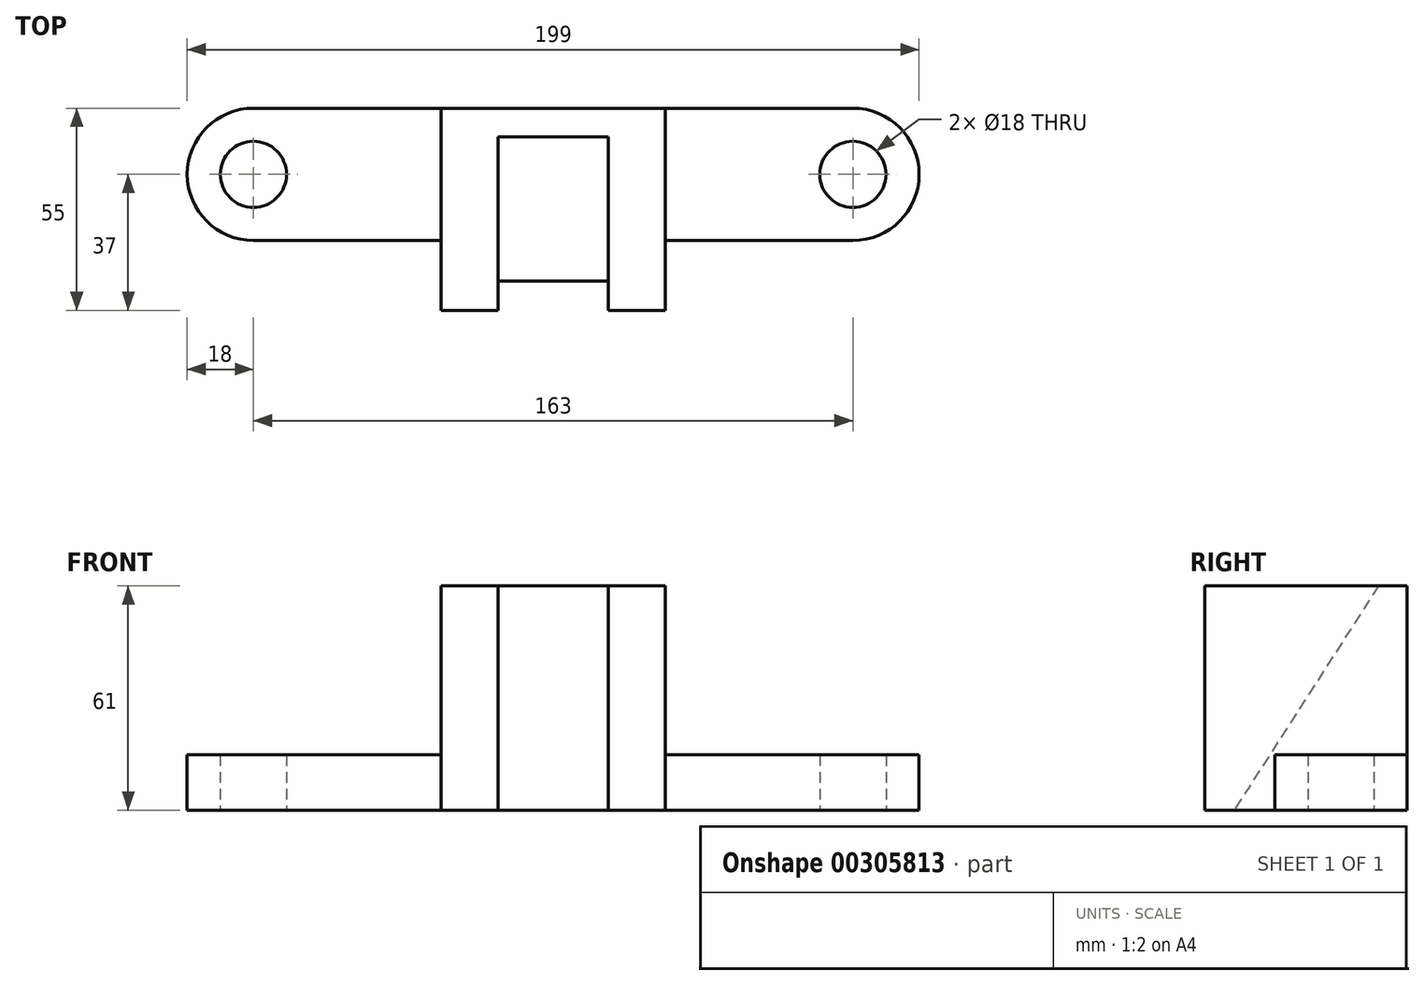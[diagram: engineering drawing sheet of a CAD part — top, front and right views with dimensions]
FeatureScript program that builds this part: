
annotation { "Feature Type Name" : "Feature", "Feature Type Description" : "" }
export const myFeature = defineFeature(function(context is Context, id is Id, definition is map)
    precondition{}
    {
        {
            var Q0;
            Q0=qCreatedBy(makeId("Top.planeOp"),FACE);
            var sketch = newSketch(context, id + "F0", { "sketchPlane" : qUnion([Q0])});
            skLineSegment(sketch, "E0.bottom", {"start": v(-30.5, 27.5) * mm, "end": v(30.5, 27.5) * mm});
            skLineSegment(sketch, "E0.top", {"start": v(-30.5, -27.5) * mm, "end": v(30.5, -27.5) * mm});
            skLineSegment(sketch, "E0.left", {"start": v(-30.5, 27.5) * mm, "end": v(-30.5, -27.5) * mm});
            skLineSegment(sketch, "E0.right", {"start": v(30.5, 27.5) * mm, "end": v(30.5, -27.5) * mm});
            skSolve(sketch);
        }
        {
            var Q0;
            Q0 = qSketchRegion(id + "F0", true);
            extrude(context, id + "F1", {"entities" : qUnion([Q0]), "depth" : 61 * mm});
        }
        {
            var Q0;
            Q0=makeQuery(id+"F1.opExtrude","CAP_FACE",FACE,{"disambiguationData":[OSD([sQuery(id+"F0.wireOp",EDGE,"E0.bottom"),sQuery(id+"F0.wireOp",EDGE,"E0.top"),sQuery(id+"F0.wireOp",EDGE,"E0.left"),sQuery(id+"F0.wireOp",EDGE,"E0.right")])],"isStart":false});
            var sketch = newSketch(context, id + "F2", { "sketchPlane" : qUnion([Q0])});
            skLineSegment(sketch, "E1.bottom", {"start": v(-15, -27.5) * mm, "end": v(15, -27.5) * mm});
            skLineSegment(sketch, "E1.top", {"start": v(-15, 19.75) * mm, "end": v(15, 19.75) * mm});
            skLineSegment(sketch, "E1.left", {"start": v(-15, -27.5) * mm, "end": v(-15, 19.75) * mm});
            skLineSegment(sketch, "E1.right", {"start": v(15, -27.5) * mm, "end": v(15, 19.75) * mm});
            skSolve(sketch);
        }
        {
            var Q0;
            Q0 = qSketchRegion(id + "F2", true);
            extrude(context, id + "F3", {"entities" : qUnion([Q0]), "operationType" : NewBodyOperationType.REMOVE, "oppositeDirection" : true, "depth" : 61 * mm});
        }
        {
            var Q0;
            Q0=makeQuery(id+"F1.opExtrude","CAP_FACE",FACE,{"disambiguationData":[OSD([sQuery(id+"F0.wireOp",EDGE,"E0.bottom"),sQuery(id+"F0.wireOp",EDGE,"E0.top"),sQuery(id+"F0.wireOp",EDGE,"E0.left"),sQuery(id+"F0.wireOp",EDGE,"E0.right")])],"isStart":true});
            var sketch = newSketch(context, id + "F4", { "sketchPlane" : qUnion([Q0])});
            skLineSegment(sketch, "E2", {"start": v(-30.5, -27.5) * mm, "end": v(-81.5, -27.5) * mm});
            skLineSegment(sketch, "E3", {"start": v(-30.5, 8.5) * mm, "end": v(-81.5, 8.5) * mm});
            skArc(sketch, "E4", {"start": v(-81.5, 8.5) * mm, "mid": v(-99.5, -9.5) * mm, "end": v(-81.5, -27.5) * mm});
            skCircle(sketch, "E5", {"center": v(-81.5, -9.5) * mm, "radius": 9 * mm});
            skLineSegment(sketch, "E6.MirrorCS", {"start": v(30.5, -27.5) * mm, "end": v(81.5, -27.5) * mm});
            skArc(sketch, "E7.MirrorCS", {"start": v(81.5, 8.5) * mm, "mid": v(99.5, -9.5) * mm, "end": v(81.5, -27.5) * mm});
            skLineSegment(sketch, "E8.MirrorCS", {"start": v(30.5, 8.5) * mm, "end": v(81.5, 8.5) * mm});
            skCircle(sketch, "E9.MirrorC", {"center": v(81.5, -9.5) * mm, "radius": 9 * mm});
            skSolve(sketch);
        }
        {
            var Q0;
            {var subQ1=sQuery(id+"F4.wireOp",EDGE,"E2");Q0=makeQuery(id+"F4.imprint","IMPRINT",FACE,{"disambiguationData":[TD([[makeQuery(id+"F4.imprint","IMPRINT",EDGE,{"derivedFrom":subQ1}),-1.0]])]});}
            var Q1;
            {var subQ1=sQuery(id+"F4.wireOp",EDGE,"E6.MirrorCS");Q1=makeQuery(id+"F4.imprint","IMPRINT",FACE,{"disambiguationData":[TD([[makeQuery(id+"F4.imprint","IMPRINT",EDGE,{"derivedFrom":subQ1}),1.0]])]});}
            extrude(context, id + "F5", {"entities" : qUnion([Q0, Q1]), "operationType" : NewBodyOperationType.ADD, "oppositeDirection" : true, "depth" : 15 * mm});
        }
        {
            var Q0;
            Q0=makeQuery(id+"F3.boolean.opBoolean","COPY",FACE,{"derivedFrom":makeQuery(id+"F3.opExtrude","SWEPT_FACE",FACE,{"disambiguationData":[OSD([sQuery(id+"F2.wireOp",EDGE,"E1.left")])]})});
            var sketch = newSketch(context, id + "F6", { "sketchPlane" : qUnion([Q0])});
            skLineSegment(sketch, "E10", {"start": v(19.75, 61) * mm, "end": v(-19.5, 0) * mm});
            skLineSegment(sketch, "E11", {"start": v(-19.5, 0) * mm, "end": v(19.75, 0) * mm});
            skLineSegment(sketch, "E12", {"start": v(19.75, 0) * mm, "end": v(19.75, 61) * mm});
            skSolve(sketch);
        }
        {
            var Q0;
            Q0 = qSketchRegion(id + "F6", true);
            extrude(context, id + "F7", {"entities" : qUnion([Q0]), "operationType" : NewBodyOperationType.ADD, "depth" : 30 * mm});
        }
    });
